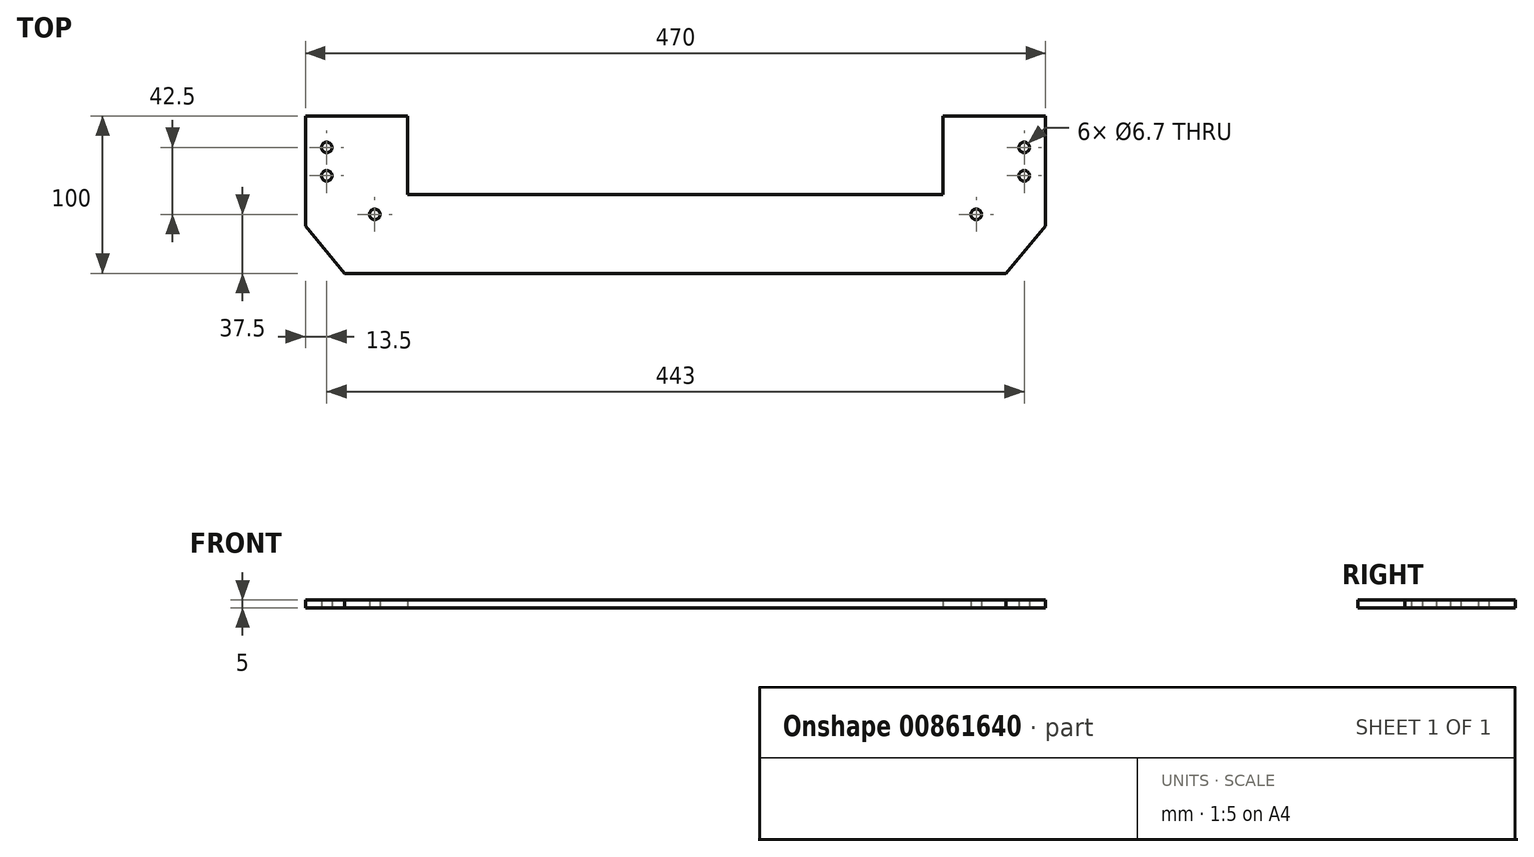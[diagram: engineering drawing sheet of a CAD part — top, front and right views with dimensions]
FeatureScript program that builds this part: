
annotation { "Feature Type Name" : "Feature", "Feature Type Description" : "" }
export const myFeature = defineFeature(function(context is Context, id is Id, definition is map)
    precondition{}
    {
        {
            var Q0;
            Q0=qCreatedBy(makeId("Top.planeOp"),FACE);
            var sketch = newSketch(context, id + "F0", { "sketchPlane" : qUnion([Q0])});
            skLineSegment(sketch, "E0", {"start": v(-210, 0) * mm, "end": v(-235, 30) * mm});
            skLineSegment(sketch, "E1", {"start": v(-235, 30) * mm, "end": v(-235, 100) * mm});
            skLineSegment(sketch, "E2", {"start": v(-235, 100) * mm, "end": v(-170, 100) * mm});
            skLineSegment(sketch, "E3", {"start": v(-170, 100) * mm, "end": v(-170, 50) * mm});
            skLineSegment(sketch, "E4", {"start": v(-170, 50) * mm, "end": v(0, 50) * mm});
            skLineSegment(sketch, "E5", {"start": v(-210, 0) * mm, "end": v(0, 0) * mm});
            skLineSegment(sketch, "E6", {"start": v(0, 50) * mm, "end": v(0, -26.87) * mm, "construction": true});
            skCircle(sketch, "E7", {"center": v(-191, 37.5) * mm, "radius": 3.35 * mm});
            skCircle(sketch, "E8", {"center": v(-221.5, 80) * mm, "radius": 3.35 * mm});
            skCircle(sketch, "E9", {"center": v(-221.5, 62) * mm, "radius": 3.35 * mm});
            skLineSegment(sketch, "E10.MirrorCS", {"start": v(210, 0) * mm, "end": v(235, 30) * mm});
            skCircle(sketch, "E11.MirrorC", {"center": v(221.5, 80) * mm, "radius": 3.35 * mm});
            skLineSegment(sketch, "E12.MirrorCS", {"start": v(170, 100) * mm, "end": v(170, 50) * mm});
            skLineSegment(sketch, "E13.MirrorCS", {"start": v(210, 0) * mm, "end": v(0, 0) * mm});
            skLineSegment(sketch, "E14.MirrorCS", {"start": v(170, 50) * mm, "end": v(0, 50) * mm});
            skCircle(sketch, "E15.MirrorC", {"center": v(191, 37.5) * mm, "radius": 3.35 * mm});
            skLineSegment(sketch, "E16.MirrorCS", {"start": v(235, 100) * mm, "end": v(170, 100) * mm});
            skLineSegment(sketch, "E17.MirrorCS", {"start": v(235, 30) * mm, "end": v(235, 100) * mm});
            skCircle(sketch, "E18.MirrorC", {"center": v(221.5, 62) * mm, "radius": 3.35 * mm});
            skSolve(sketch);
        }
        {
            var Q0;
            Q0 = qSketchRegion(id + "F0", true);
            extrude(context, id + "F1", {"entities" : qUnion([Q0]), "depth" : 5 * mm, "offsetDistance" : 25 * mm});
        }
    });
